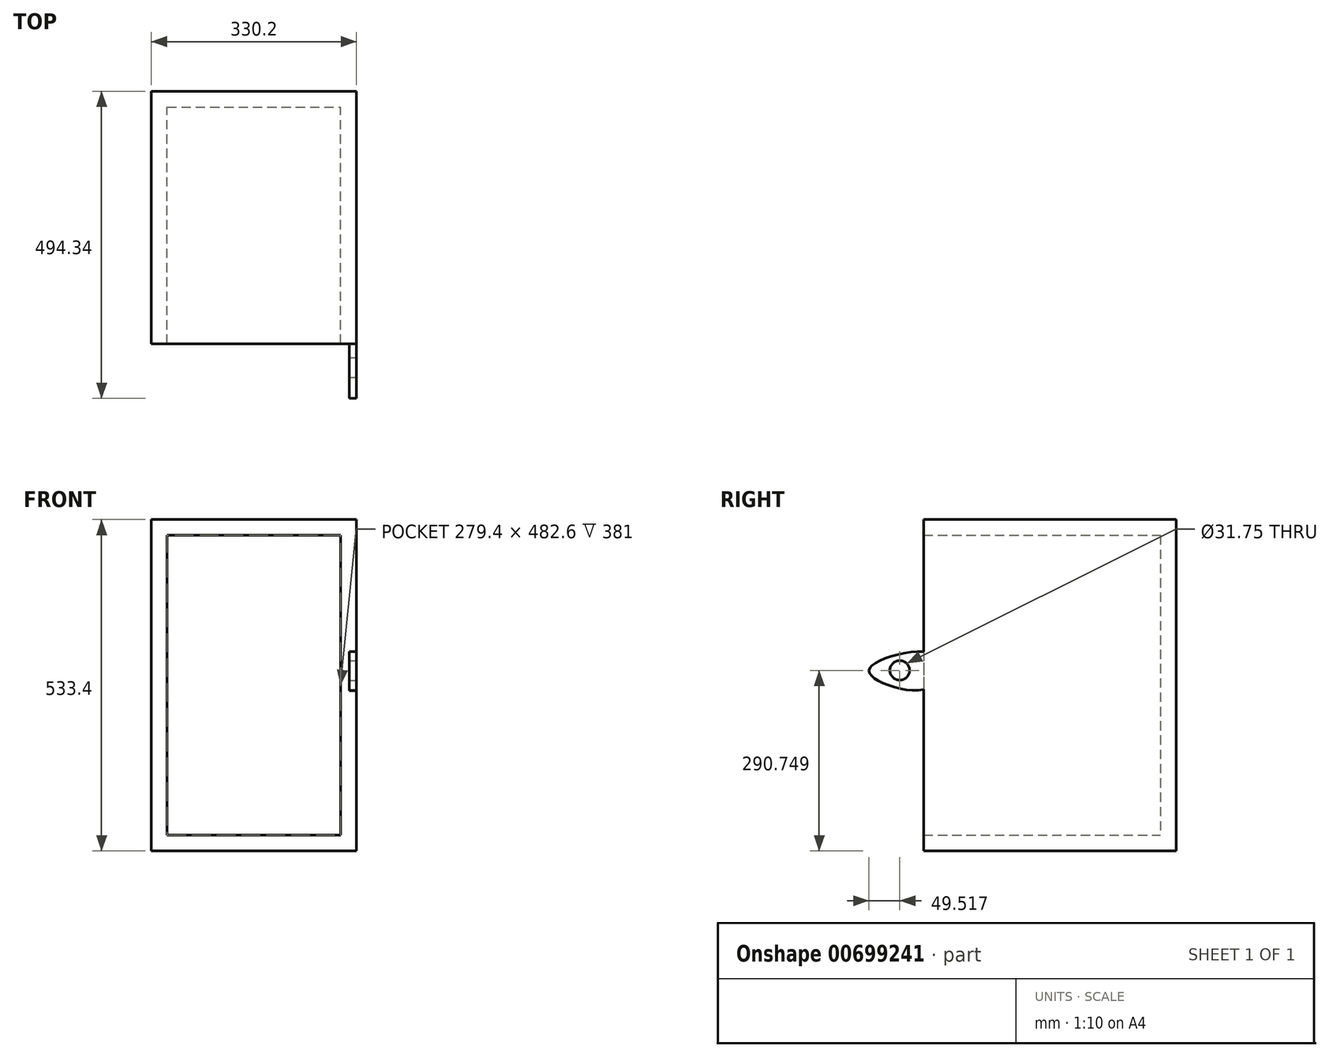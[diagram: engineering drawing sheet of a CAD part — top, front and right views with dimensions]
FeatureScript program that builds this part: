
annotation { "Feature Type Name" : "Feature", "Feature Type Description" : "" }
export const myFeature = defineFeature(function(context is Context, id is Id, definition is map)
    precondition{}
    {
        {
            var Q0;
            Q0=qCreatedBy(makeId("Front.planeOp"),FACE);
            var sketch = newSketch(context, id + "F0", { "sketchPlane" : qUnion([Q0])});
            skLineSegment(sketch, "E0.bottom", {"start": v(-139.7, 241.3) * mm, "end": v(139.7, 241.3) * mm});
            skLineSegment(sketch, "E0.top", {"start": v(-139.7, -241.3) * mm, "end": v(139.7, -241.3) * mm});
            skLineSegment(sketch, "E0.left", {"start": v(-139.7, 241.3) * mm, "end": v(-139.7, -241.3) * mm});
            skLineSegment(sketch, "E0.right", {"start": v(139.7, 241.3) * mm, "end": v(139.7, -241.3) * mm});
            skPoint(sketch, "E0.middle", {"position": v(0, 0) * mm});
            skPoint(sketch, "E1.left.start.orphan", {"position": v(-151.86, 252.88) * mm});
            skPoint(sketch, "E1.right.start.orphan", {"position": v(151.86, 252.88) * mm});
            skPoint(sketch, "E1.top.end.orphan", {"position": v(151.86, -252.88) * mm});
            skPoint(sketch, "E1.top.start.orphan", {"position": v(-151.86, -252.88) * mm});
            skPoint(sketch, "E2.bottom.start.orphan", {"position": v(-165.1, 266.7) * mm});
            skPoint(sketch, "E2.right.start.orphan", {"position": v(165.1, 266.7) * mm});
            skPoint(sketch, "E2.top.end.orphan", {"position": v(165.1, -266.7) * mm});
            skPoint(sketch, "E2.top.start.orphan", {"position": v(-165.1, -266.7) * mm});
            skPoint(sketch, "E3.right.start.orphan", {"position": v(190.5, 292.1) * mm});
            skPoint(sketch, "E3.top.end.orphan", {"position": v(190.5, -292.1) * mm});
            skPoint(sketch, "E3.left.end.orphan", {"position": v(-190.5, -292.1) * mm});
            skPoint(sketch, "E3.left.start.orphan", {"position": v(-190.5, 292.1) * mm});
            skLineSegment(sketch, "E4.bottom", {"start": v(165.1, 266.7) * mm, "end": v(-165.1, 266.7) * mm});
            skLineSegment(sketch, "E4.top", {"start": v(165.1, -266.7) * mm, "end": v(-165.1, -266.7) * mm});
            skLineSegment(sketch, "E4.left", {"start": v(165.1, 266.7) * mm, "end": v(165.1, -266.7) * mm});
            skLineSegment(sketch, "E4.right", {"start": v(-165.1, 266.7) * mm, "end": v(-165.1, -266.7) * mm});
            skSolve(sketch);
        }
        {
            var Q0;
            Q0=makeQuery(id+"F0.imprint","IMPRINT",FACE,{"disambiguationData":[TD([[makeQuery(id+"F0.imprint","IMPRINT",EDGE,{"derivedFrom":sQuery(id+"F0.wireOp",EDGE,"E0.bottom")}),1.0]])]});
            extrude(context, id + "F1", {"entities" : qUnion([Q0]), "depth" : 381 * mm, "offsetDistance" : 25.4 * mm});
        }
        {
            var Q0;
            Q0=makeQuery(id+"F1.opExtrude","SWEPT_FACE",FACE,{"disambiguationData":[OSD([sQuery(id+"F0.wireOp",EDGE,"E4.left")])]});
            var sketch = newSketch(context, id + "F2", { "sketchPlane" : qUnion([Q0])});
            skPoint(sketch, "E5.0.internal.snap0", {"position": v(-381, 0) * mm});
            skPoint(sketch, "E5.1.internal.snap0", {"position": v(-381, 0) * mm});
            skFitSpline(sketch, "E5", {"points": [v(-367.4, 0) * mm, v(-436.87, 0) * mm, v(-468.93, 22.98) * mm, v(-436.87, 45.43) * mm, v(-359.91, 45.43) * mm, v(-367.4, 0) * mm]});
            skSolve(sketch);
        }
        {
            var Q0;
            {var subQ0=sQuery(id+"F2.wireOp",EDGE,"E5");var subQ1=makeQuery(id+"F1.opExtrude","CAP_EDGE",EDGE,{"disambiguationData":[OSD([sQuery(id+"F0.wireOp",EDGE,"E4.left")])],"isStart":false});var subQ2=makeQuery(id+"F2.imprint","INTERSECT",VERTEX,{"disambiguationData":[OD(0.0)],"derivedFrom":[subQ1,subQ0]});Q0=makeQuery(id+"F2.imprint","IMPRINT",FACE,{"disambiguationData":[TD([[makeQuery(id+"F2.imprint","IMPRINT",EDGE,{"disambiguationData":[TD([[subQ2,1.0]])],"derivedFrom":subQ0}),-1.0]])]});}
            var Q1;
            {var subQ0=sQuery(id+"F2.wireOp",EDGE,"E5");var subQ1=makeQuery(id+"F1.opExtrude","CAP_EDGE",EDGE,{"disambiguationData":[OSD([sQuery(id+"F0.wireOp",EDGE,"E4.left")])],"isStart":false});var subQ2=makeQuery(id+"F2.imprint","INTERSECT",VERTEX,{"disambiguationData":[OD(0.0)],"derivedFrom":[subQ1,subQ0]});Q1=makeQuery(id+"F2.imprint","IMPRINT",FACE,{"disambiguationData":[TD([[makeQuery(id+"F2.imprint","IMPRINT",EDGE,{"disambiguationData":[TD([[subQ2,-1.0]])],"derivedFrom":subQ0}),-1.0]])]});}
            extrude(context, id + "F3", {"entities" : qUnion([Q0, Q1]), "operationType" : NewBodyOperationType.ADD, "oppositeDirection" : true, "depth" : 11.43 * mm, "offsetDistance" : 25.4 * mm});
        }
        {
            var Q0;
            Q0=makeQuery(id+"F3.boolean.opBoolean","MERGE",FACE,{"derivedFrom":[makeQuery(id+"F1.opExtrude","SWEPT_FACE",FACE,{"disambiguationData":[OSD([sQuery(id+"F0.wireOp",EDGE,"E4.left")])]}),makeQuery(id+"F3.opExtrude","CAP_FACE",FACE,{"disambiguationData":[OSD([sQuery(id+"F2.wireOp",EDGE,"E5")])],"isStart":true})]});
            var sketch = newSketch(context, id + "F4", { "sketchPlane" : qUnion([Q0])});
            skCircle(sketch, "E6", {"center": v(-419.42, 24.05) * mm, "radius": 17.53 * mm});
            skSolve(sketch);
        }
        {
            var Q0;
            Q0=sQuery(id+"F4.wireOp",VERTEX,"E6.center");
            var Q1;
            Q1=makeQuery(id+"F1.opExtrude","SWEPT_BODY",BODY,{"disambiguationData":[OSD([sQuery(id+"F0.wireOp",EDGE,"E0.bottom"),sQuery(id+"F0.wireOp",EDGE,"E0.top"),sQuery(id+"F0.wireOp",EDGE,"E0.left"),sQuery(id+"F0.wireOp",EDGE,"E0.right"),sQuery(id+"F0.wireOp",EDGE,"E4.bottom"),sQuery(id+"F0.wireOp",EDGE,"E4.top"),sQuery(id+"F0.wireOp",EDGE,"E4.left"),sQuery(id+"F0.wireOp",EDGE,"E4.right")])]});
            hole(context, id + "F5", {"style" : HoleStyle.SIMPLE, "endStyle" : HoleEndStyle.THROUGH, "holeDiameter" : 31.75 * mm, "majorDiameter" : 6.35 * mm, "isTappedThrough" : true, "tappedDepth" : 12.7 * mm, "tapClearance" : 3, "locations" : qUnion([Q0]), "scope" : qUnion([Q1])});
        }
        {
            var Q0;
            Q0=makeQuery(id+"F1.opExtrude","CAP_FACE",FACE,{"disambiguationData":[OSD([sQuery(id+"F0.wireOp",EDGE,"E0.bottom"),sQuery(id+"F0.wireOp",EDGE,"E0.top"),sQuery(id+"F0.wireOp",EDGE,"E0.left"),sQuery(id+"F0.wireOp",EDGE,"E0.right"),sQuery(id+"F0.wireOp",EDGE,"E4.bottom"),sQuery(id+"F0.wireOp",EDGE,"E4.top"),sQuery(id+"F0.wireOp",EDGE,"E4.left"),sQuery(id+"F0.wireOp",EDGE,"E4.right")])],"isStart":true});
            var sketch = newSketch(context, id + "F6", { "sketchPlane" : qUnion([Q0])});
            skLineSegment(sketch, "E7.bottom", {"start": v(-165.1, 266.7) * mm, "end": v(165.1, 266.7) * mm});
            skLineSegment(sketch, "E7.top", {"start": v(-165.1, -266.7) * mm, "end": v(165.1, -266.7) * mm});
            skLineSegment(sketch, "E7.left", {"start": v(-165.1, 266.7) * mm, "end": v(-165.1, -266.7) * mm});
            skLineSegment(sketch, "E7.right", {"start": v(165.1, 266.7) * mm, "end": v(165.1, -266.7) * mm});
            skSolve(sketch);
        }
        {
            var Q0;
            Q0 = qSketchRegion(id + "F6", true);
            extrude(context, id + "F7", {"entities" : qUnion([Q0]), "operationType" : NewBodyOperationType.ADD, "depth" : 25.4 * mm, "offsetDistance" : 25.4 * mm});
        }
    });
